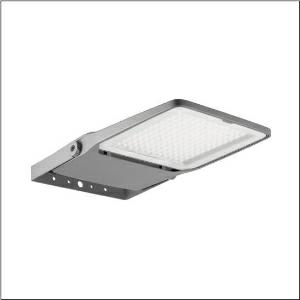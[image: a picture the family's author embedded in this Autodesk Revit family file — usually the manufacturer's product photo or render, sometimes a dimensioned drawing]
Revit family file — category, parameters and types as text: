
# Revit family: floodlight_fl_20_midi___rs17_5xa7682e2b2ac_f397
name_source: partatom
category: Lighting Fixtures
units: mm (PartAtom-declared; Revit-internal decimal feet)

## family parameters
Cut with Voids When Loaded = No
Host = Face
Light Source = No
Part Type = Normal
Room Calculation Point = No
Round Connector Dimension = Use Diameter
Shared = No

## types (1)
- --- (1 x LED 4000K / CRI = 70 (unbekannt), 29150 lm, 4000K)
    Apparent Load = 208 VA
    CIE Flux Codes = 79 92 99 100 100
    Color Rendering = 70
    Color Temperature = 4000K
    Default Elevation = 1800 mm
    Description = Floodlight FL 20 midi, floodlight, primary light control with lens, of plastic, primary optical cover: protective disc, of toughened safety glass, transparent, light distribution: RS17, light emission: direct distribution, primary light characteristic: rotationally symmetric, installation type: surface-mounted, LED High Power LED, rated luminous flux: 29.150 lm, light colour: 740, colour temperature: 4000K, control gear: ECG Plus, control: flexible luminous flux parameterisation, time-dependent luminous flux control, digital communication interface, power reduction, overheat protection, electronic power reduction, with terminal, 5-pole, max. 2.5mm², mains connection: 220..240V, AC, 50/60Hz, rated input power: 208W, LED unit, of diecast aluminium, powder-coated, Siteco® metallic grey (DB 702S), length: 731 mm, width: 450 mm, height: 76mm, housing frame, of diecast aluminium, powder-coated, Siteco® metallic grey (DB 702S), wall fastening, of steel, powder-coated, Siteco® metallic grey (DB 702S), DALIprotection rating (complete): IP66, insulation class (complete): insulation class II (safety insulation), certification: CE, ENEC, VDE, protection symbol: D, permissible ambient temperature for indoor applications: -40..+40°C, permissible ambient temperature for outdoor applications: -40..+50°C, standard: DIN EN 12944, packaging unit: 1 piece

Light Distribution: RS17
    Height = 76 mm
    Lamp = 1 x LED 4000K / CRI >= 70 (unbekannt)
    Lamp Light Flux = 29150 lm
    Lamp count = 1
    Length = 731 mm
    Luminous efficacy = 140 lm/W
    Manufacturer = Siteco
    ModVariant = No
    Model = 5XA7682E2B2AC
    Number of Poles = 1
    OnlyDefault = Yes
    Power Factor = 1
    Product Name = Floodlight FL 20 midi | RS17
    Product group = floodlight | pylon top
    ProductGroupID = 6101
    Protection Class = Protection class II
    Protection Degree = IP 66
    RLX_Detail_Level = 1
    RlxData = <blob elided: 86557 chars, md5=21a992e6>
    Socket = socket
    Standby Power = 0 W
    System Light Flux = 29150 lm
    System Power = 208 W
    Type Comments = factory setting: luminous flux: 100 % | dim-lin: 254 | 484 mA
    Type Image = l_1005944.jpg
    URL = http://relux.com
    VarID = @adj_141777
    Voltage = 0 V
    Weight = 0.00 kg
    Width = 450 mm

## geometry (parser evidence)
native form markers: Blend x4, Sweep x14
no freeform markers — native parametric forms only
